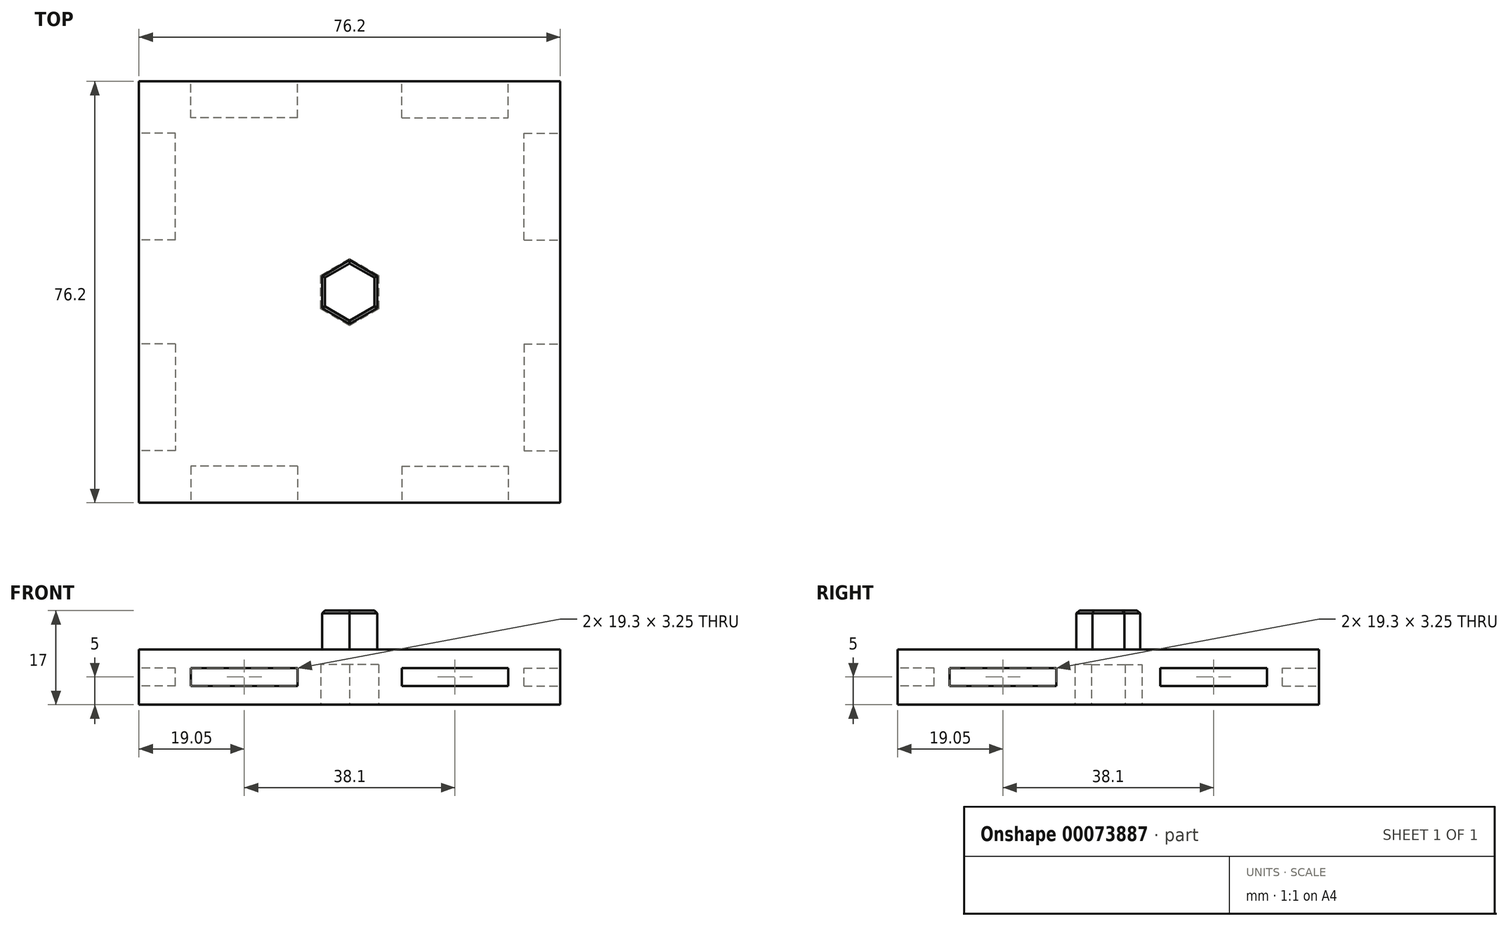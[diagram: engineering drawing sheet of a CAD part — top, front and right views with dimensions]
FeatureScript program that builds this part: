
annotation { "Feature Type Name" : "Feature", "Feature Type Description" : "" }
export const myFeature = defineFeature(function(context is Context, id is Id, definition is map)
    precondition{}
    {
        {
            var Q0;
            Q0=qCreatedBy(makeId("Top.planeOp"),FACE);
            var sketch = newSketch(context, id + "F0", { "sketchPlane" : qUnion([Q0])});
            skLineSegment(sketch, "E0.rect.bottom", {"start": v(38.1, -38.1) * mm, "end": v(-38.1, -38.1) * mm});
            skLineSegment(sketch, "E0.rect.top", {"start": v(38.1, 38.1) * mm, "end": v(-38.1, 38.1) * mm});
            skLineSegment(sketch, "E0.rect.left", {"start": v(38.1, -38.1) * mm, "end": v(38.1, 38.1) * mm});
            skLineSegment(sketch, "E0.rect.right", {"start": v(-38.1, -38.1) * mm, "end": v(-38.1, 38.1) * mm});
            skPoint(sketch, "E0.rect.middle", {"position": v(0, 0) * mm});
            skSolve(sketch);
        }
        {
            var Q0;
            Q0=makeQuery(id+"F0.imprint","IMPRINT",FACE,{"disambiguationData":[TD([[makeQuery(id+"F0.imprint","IMPRINT",EDGE,{"derivedFrom":sQuery(id+"F0.wireOp",EDGE,"E0.rect.bottom")}),-1.0]])]});
            extrude(context, id + "F1", {"entities" : qUnion([Q0]), "depth" : 10 * mm});
        }
        {
            var Q0;
            Q0=makeQuery(id+"F1.opExtrude","CAP_FACE",FACE,{"disambiguationData":[OSD([sQuery(id+"F0.wireOp",EDGE,"E0.rect.bottom"),sQuery(id+"F0.wireOp",EDGE,"E0.rect.top"),sQuery(id+"F0.wireOp",EDGE,"E0.rect.left"),sQuery(id+"F0.wireOp",EDGE,"E0.rect.right")])],"isStart":false});
            var sketch = newSketch(context, id + "F2", { "sketchPlane" : qUnion([Q0])});
            skCircle(sketch, "E1.cCircle", {"center": v(0, 0) * mm, "radius": 5 * mm, "construction": true});
            skLineSegment(sketch, "E1.0", {"start": v(5, 2.89) * mm, "end": v(5, -2.89) * mm});
            skLineSegment(sketch, "E1.1", {"start": v(5, -2.89) * mm, "end": v(0, -5.77) * mm});
            skLineSegment(sketch, "E1.2", {"start": v(0, -5.77) * mm, "end": v(-5, -2.89) * mm});
            skLineSegment(sketch, "E1.3", {"start": v(-5, -2.89) * mm, "end": v(-5, 2.89) * mm});
            skLineSegment(sketch, "E1.4", {"start": v(-5, 2.89) * mm, "end": v(0, 5.77) * mm});
            skLineSegment(sketch, "E1.5", {"start": v(0, 5.77) * mm, "end": v(5, 2.89) * mm});
            skPoint(sketch, "E1.0.midPoint", {"position": v(5, 0) * mm});
            skSolve(sketch);
        }
        {
            var Q0;
            Q0=makeQuery(id+"F2.imprint","IMPRINT",FACE,{"disambiguationData":[TD([[makeQuery(id+"F2.imprint","IMPRINT",EDGE,{"derivedFrom":sQuery(id+"F2.wireOp",EDGE,"E1.0")}),-1.0]])]});
            extrude(context, id + "F3", {"entities" : qUnion([Q0]), "operationType" : NewBodyOperationType.ADD, "depth" : 7 * mm});
        }
        {
            var Q0;
            Q0=makeQuery(id+"F1.opExtrude","CAP_FACE",FACE,{"disambiguationData":[OSD([sQuery(id+"F0.wireOp",EDGE,"E0.rect.bottom"),sQuery(id+"F0.wireOp",EDGE,"E0.rect.top"),sQuery(id+"F0.wireOp",EDGE,"E0.rect.left"),sQuery(id+"F0.wireOp",EDGE,"E0.rect.right")])],"isStart":true});
            var sketch = newSketch(context, id + "F4", { "sketchPlane" : qUnion([Q0])});
            skCircle(sketch, "E2.0", {"center": v(0, 0) * mm, "radius": 5 * mm, "construction": true});
            skLineSegment(sketch, "E2.1", {"start": v(5, -2.89) * mm, "end": v(5, 2.89) * mm, "construction": true});
            skLineSegment(sketch, "E2.2", {"start": v(5, 2.89) * mm, "end": v(0, 5.77) * mm, "construction": true});
            skLineSegment(sketch, "E2.3", {"start": v(0, 5.77) * mm, "end": v(-5, 2.89) * mm, "construction": true});
            skLineSegment(sketch, "E2.4", {"start": v(-5, 2.89) * mm, "end": v(-5, -2.89) * mm, "construction": true});
            skLineSegment(sketch, "E2.5", {"start": v(-5, -2.89) * mm, "end": v(0, -5.77) * mm, "construction": true});
            skLineSegment(sketch, "E2.6", {"start": v(0, -5.77) * mm, "end": v(5, -2.89) * mm, "construction": true});
            skPoint(sketch, "E2.7", {"position": v(5, 0) * mm});
            skLineSegment(sketch, "E3.0", {"start": v(5.25, 3.03) * mm, "end": v(0, 6.06) * mm});
            skLineSegment(sketch, "E3.1", {"start": v(-5.25, 3.03) * mm, "end": v(-5.25, -3.03) * mm});
            skLineSegment(sketch, "E3.2", {"start": v(-5.25, -3.03) * mm, "end": v(0, -6.06) * mm});
            skLineSegment(sketch, "E3.3", {"start": v(0, 6.06) * mm, "end": v(-5.25, 3.03) * mm});
            skLineSegment(sketch, "E3.4", {"start": v(0, -6.06) * mm, "end": v(5.25, -3.03) * mm});
            skLineSegment(sketch, "E3.5", {"start": v(5.25, -3.03) * mm, "end": v(5.25, 3.03) * mm});
            skSolve(sketch);
        }
        {
            var Q0;
            Q0 = qSketchRegion(id + "F4", true);
            extrude(context, id + "F5", {"entities" : qUnion([Q0]), "operationType" : NewBodyOperationType.REMOVE, "oppositeDirection" : true, "depth" : 7.25 * mm});
        }
        {
            var Q0;
            Q0=makeQuery(id+"F1.opExtrude","SWEPT_FACE",FACE,{"disambiguationData":[OSD([sQuery(id+"F0.wireOp",EDGE,"E0.rect.bottom")])]});
            var sketch = newSketch(context, id + "F6", { "sketchPlane" : qUnion([Q0])});
            skLineSegment(sketch, "E4", {"start": v(0, 0) * mm, "end": v(0, 5) * mm, "construction": true});
            skLineSegment(sketch, "E5", {"start": v(-6.35, 5) * mm, "end": v(6.35, 5) * mm, "construction": true});
            skLineSegment(sketch, "E6.rect.bottom", {"start": v(-6.35, 0) * mm, "end": v(-31.75, 0) * mm, "construction": true});
            skLineSegment(sketch, "E6.rect.top", {"start": v(-6.35, 10) * mm, "end": v(-31.75, 10) * mm, "construction": true});
            skLineSegment(sketch, "E6.rect.left", {"start": v(-6.35, 0) * mm, "end": v(-6.35, 10) * mm, "construction": true});
            skLineSegment(sketch, "E6.rect.right", {"start": v(-31.75, 0) * mm, "end": v(-31.75, 10) * mm, "construction": true});
            skPoint(sketch, "E6.rect.middle", {"position": v(-19.05, 5) * mm});
            skLineSegment(sketch, "E7", {"start": v(-44.45, 5) * mm, "end": v(-31.75, 5) * mm, "construction": true});
            skPoint(sketch, "E8", {"position": v(-38.1, 5) * mm});
            skLineSegment(sketch, "E9.rect.bottom", {"start": v(-9.4, 3.37) * mm, "end": v(-28.7, 3.37) * mm});
            skLineSegment(sketch, "E9.rect.top", {"start": v(-9.4, 6.62) * mm, "end": v(-28.7, 6.63) * mm});
            skLineSegment(sketch, "E9.rect.left", {"start": v(-9.4, 3.37) * mm, "end": v(-9.4, 6.62) * mm});
            skLineSegment(sketch, "E9.rect.right", {"start": v(-28.7, 3.37) * mm, "end": v(-28.7, 6.62) * mm});
            skPoint(sketch, "E10.MirrorP", {"position": v(19.05, 5) * mm});
            skLineSegment(sketch, "E11.MirrorCS", {"start": v(28.7, 3.37) * mm, "end": v(28.7, 6.62) * mm});
            skLineSegment(sketch, "E12.MirrorCS", {"start": v(9.4, 3.37) * mm, "end": v(9.4, 6.62) * mm});
            skLineSegment(sketch, "E13.MirrorCS", {"start": v(9.4, 3.37) * mm, "end": v(28.7, 3.37) * mm});
            skLineSegment(sketch, "E14.MirrorCS", {"start": v(9.4, 6.62) * mm, "end": v(28.7, 6.63) * mm});
            skSolve(sketch);
        }
        {
            var Q0;
            Q0=qCreatedBy(makeId("Front.planeOp"),FACE);
            var sketch = newSketch(context, id + "F7", { "sketchPlane" : qUnion([Q0])});
            skLineSegment(sketch, "E15", {"start": v(0, 40.14) * mm, "end": v(0, 0) * mm, "construction": true});
            skSolve(sketch);
        }
        {
            var Q0;
            Q0 = qSketchRegion(id + "F6", true);
            extrude(context, id + "F8", {"entities" : qUnion([Q0]), "oppositeDirection" : true, "depth" : 6.35 * mm + .25 * mm});
        }
        {
            var Q0;
            Q0=makeQuery(id+"F8.opExtrude","SWEPT_BODY",BODY,{"disambiguationData":[OSD([sQuery(id+"F6.wireOp",EDGE,"E11.MirrorCS"),sQuery(id+"F6.wireOp",EDGE,"E12.MirrorCS"),sQuery(id+"F6.wireOp",EDGE,"E13.MirrorCS"),sQuery(id+"F6.wireOp",EDGE,"E14.MirrorCS")])]});
            var Q1;
            Q1=makeQuery(id+"F8.opExtrude","SWEPT_BODY",BODY,{"disambiguationData":[OSD([sQuery(id+"F6.wireOp",EDGE,"E9.rect.bottom"),sQuery(id+"F6.wireOp",EDGE,"E9.rect.top"),sQuery(id+"F6.wireOp",EDGE,"E9.rect.left"),sQuery(id+"F6.wireOp",EDGE,"E9.rect.right")])]});
            var Q2;
            Q2=sQuery(id+"F7.wireOp",EDGE,"E15");
            circularPattern(context, id + "F9", {"entities" : qUnion([Q0, Q1]), "axis" : qUnion([Q2]), "angle" : 90 * degree, "instanceCount" : 4});
        }
        {
            var Q0;
            Q0=makeQuery(id+"F9.opPattern","COPY",BODY,{"derivedFrom":makeQuery(id+"F8.opExtrude","SWEPT_BODY",BODY,{"disambiguationData":[OSD([sQuery(id+"F6.wireOp",EDGE,"E11.MirrorCS"),sQuery(id+"F6.wireOp",EDGE,"E12.MirrorCS"),sQuery(id+"F6.wireOp",EDGE,"E13.MirrorCS"),sQuery(id+"F6.wireOp",EDGE,"E14.MirrorCS")])]}),"instanceName":"3"});
            var Q1;
            Q1=makeQuery(id+"F9.opPattern","COPY",BODY,{"derivedFrom":makeQuery(id+"F8.opExtrude","SWEPT_BODY",BODY,{"disambiguationData":[OSD([sQuery(id+"F6.wireOp",EDGE,"E9.rect.bottom"),sQuery(id+"F6.wireOp",EDGE,"E9.rect.top"),sQuery(id+"F6.wireOp",EDGE,"E9.rect.left"),sQuery(id+"F6.wireOp",EDGE,"E9.rect.right")])]}),"instanceName":"3"});
            var Q2;
            Q2=makeQuery(id+"F9.opPattern","COPY",BODY,{"derivedFrom":makeQuery(id+"F8.opExtrude","SWEPT_BODY",BODY,{"disambiguationData":[OSD([sQuery(id+"F6.wireOp",EDGE,"E11.MirrorCS"),sQuery(id+"F6.wireOp",EDGE,"E12.MirrorCS"),sQuery(id+"F6.wireOp",EDGE,"E13.MirrorCS"),sQuery(id+"F6.wireOp",EDGE,"E14.MirrorCS")])]}),"instanceName":"2"});
            var Q3;
            Q3=makeQuery(id+"F9.opPattern","COPY",BODY,{"derivedFrom":makeQuery(id+"F8.opExtrude","SWEPT_BODY",BODY,{"disambiguationData":[OSD([sQuery(id+"F6.wireOp",EDGE,"E9.rect.bottom"),sQuery(id+"F6.wireOp",EDGE,"E9.rect.top"),sQuery(id+"F6.wireOp",EDGE,"E9.rect.left"),sQuery(id+"F6.wireOp",EDGE,"E9.rect.right")])]}),"instanceName":"2"});
            var Q4;
            Q4=makeQuery(id+"F9.opPattern","COPY",BODY,{"derivedFrom":makeQuery(id+"F8.opExtrude","SWEPT_BODY",BODY,{"disambiguationData":[OSD([sQuery(id+"F6.wireOp",EDGE,"E11.MirrorCS"),sQuery(id+"F6.wireOp",EDGE,"E12.MirrorCS"),sQuery(id+"F6.wireOp",EDGE,"E13.MirrorCS"),sQuery(id+"F6.wireOp",EDGE,"E14.MirrorCS")])]}),"instanceName":"1"});
            var Q5;
            Q5=makeQuery(id+"F9.opPattern","COPY",BODY,{"derivedFrom":makeQuery(id+"F8.opExtrude","SWEPT_BODY",BODY,{"disambiguationData":[OSD([sQuery(id+"F6.wireOp",EDGE,"E9.rect.bottom"),sQuery(id+"F6.wireOp",EDGE,"E9.rect.top"),sQuery(id+"F6.wireOp",EDGE,"E9.rect.left"),sQuery(id+"F6.wireOp",EDGE,"E9.rect.right")])]}),"instanceName":"1"});
            var Q6;
            Q6=makeQuery(id+"F8.opExtrude","SWEPT_BODY",BODY,{"disambiguationData":[OSD([sQuery(id+"F6.wireOp",EDGE,"E11.MirrorCS"),sQuery(id+"F6.wireOp",EDGE,"E12.MirrorCS"),sQuery(id+"F6.wireOp",EDGE,"E13.MirrorCS"),sQuery(id+"F6.wireOp",EDGE,"E14.MirrorCS")])]});
            var Q7;
            Q7=makeQuery(id+"F8.opExtrude","SWEPT_BODY",BODY,{"disambiguationData":[OSD([sQuery(id+"F6.wireOp",EDGE,"E9.rect.bottom"),sQuery(id+"F6.wireOp",EDGE,"E9.rect.top"),sQuery(id+"F6.wireOp",EDGE,"E9.rect.left"),sQuery(id+"F6.wireOp",EDGE,"E9.rect.right")])]});
            var Q8;
            Q8=makeQuery(id+"F1.opExtrude","SWEPT_BODY",BODY,{"disambiguationData":[OSD([sQuery(id+"F0.wireOp",EDGE,"E0.rect.bottom"),sQuery(id+"F0.wireOp",EDGE,"E0.rect.top"),sQuery(id+"F0.wireOp",EDGE,"E0.rect.left"),sQuery(id+"F0.wireOp",EDGE,"E0.rect.right")])]});
            booleanBodies(context, id + "F10", {"operationType" : BooleanOperationType.SUBTRACTION, "tools" : qUnion([Q0, Q1, Q2, Q3, Q4, Q5, Q6, Q7]), "targets" : qUnion([Q8])});
        }
        {
            var Q0;
            Q0=makeQuery(id+"F3.opExtrude","CAP_FACE",FACE,{"disambiguationData":[OSD([sQuery(id+"F2.wireOp",EDGE,"E1.0"),sQuery(id+"F2.wireOp",EDGE,"E1.1"),sQuery(id+"F2.wireOp",EDGE,"E1.2"),sQuery(id+"F2.wireOp",EDGE,"E1.3"),sQuery(id+"F2.wireOp",EDGE,"E1.4"),sQuery(id+"F2.wireOp",EDGE,"E1.5")])],"isStart":false});
            var Q1;
            Q1=makeQuery(id+"F5.boolean.opBoolean","COPY",EDGE,{"derivedFrom":makeQuery(id+"F5.opExtrude","CAP_EDGE",EDGE,{"disambiguationData":[OSD([sQuery(id+"F4.wireOp",EDGE,"E3.4")])],"isStart":true})});
            var Q2;
            Q2=makeQuery(id+"F5.boolean.opBoolean","COPY",EDGE,{"derivedFrom":makeQuery(id+"F5.opExtrude","CAP_EDGE",EDGE,{"disambiguationData":[OSD([sQuery(id+"F4.wireOp",EDGE,"E3.5")])],"isStart":true})});
            var Q3;
            Q3=makeQuery(id+"F5.boolean.opBoolean","COPY",EDGE,{"derivedFrom":makeQuery(id+"F5.opExtrude","CAP_EDGE",EDGE,{"disambiguationData":[OSD([sQuery(id+"F4.wireOp",EDGE,"E3.0")])],"isStart":true})});
            var Q4;
            Q4=makeQuery(id+"F5.boolean.opBoolean","COPY",EDGE,{"derivedFrom":makeQuery(id+"F5.opExtrude","CAP_EDGE",EDGE,{"disambiguationData":[OSD([sQuery(id+"F4.wireOp",EDGE,"E3.3")])],"isStart":true})});
            var Q5;
            Q5=makeQuery(id+"F5.boolean.opBoolean","COPY",EDGE,{"derivedFrom":makeQuery(id+"F5.opExtrude","CAP_EDGE",EDGE,{"disambiguationData":[OSD([sQuery(id+"F4.wireOp",EDGE,"E3.1")])],"isStart":true})});
            var Q6;
            Q6=makeQuery(id+"F5.boolean.opBoolean","COPY",EDGE,{"derivedFrom":makeQuery(id+"F5.opExtrude","CAP_EDGE",EDGE,{"disambiguationData":[OSD([sQuery(id+"F4.wireOp",EDGE,"E3.2")])],"isStart":true})});
            var Q7;
            Q7=makeQuery(id+"F10.opBoolean","COPY",EDGE,{"derivedFrom":makeQuery(id+"F9.opPattern","COPY",EDGE,{"derivedFrom":makeQuery(id+"F8.opExtrude","CAP_EDGE",EDGE,{"disambiguationData":[OSD([sQuery(id+"F6.wireOp",EDGE,"E9.rect.top")])],"isStart":true}),"instanceName":"3"})});
            var Q8;
            Q8=makeQuery(id+"F10.opBoolean","COPY",EDGE,{"derivedFrom":makeQuery(id+"F9.opPattern","COPY",EDGE,{"derivedFrom":makeQuery(id+"F8.opExtrude","CAP_EDGE",EDGE,{"disambiguationData":[OSD([sQuery(id+"F6.wireOp",EDGE,"E9.rect.left")])],"isStart":true}),"instanceName":"3"})});
            var Q9;
            Q9=makeQuery(id+"F10.opBoolean","COPY",EDGE,{"derivedFrom":makeQuery(id+"F9.opPattern","COPY",EDGE,{"derivedFrom":makeQuery(id+"F8.opExtrude","CAP_EDGE",EDGE,{"disambiguationData":[OSD([sQuery(id+"F6.wireOp",EDGE,"E9.rect.bottom")])],"isStart":true}),"instanceName":"3"})});
            var Q10;
            Q10=makeQuery(id+"F10.opBoolean","COPY",EDGE,{"derivedFrom":makeQuery(id+"F9.opPattern","COPY",EDGE,{"derivedFrom":makeQuery(id+"F8.opExtrude","CAP_EDGE",EDGE,{"disambiguationData":[OSD([sQuery(id+"F6.wireOp",EDGE,"E9.rect.right")])],"isStart":true}),"instanceName":"3"})});
            var Q11;
            Q11=makeQuery(id+"F10.opBoolean","COPY",EDGE,{"derivedFrom":makeQuery(id+"F9.opPattern","COPY",EDGE,{"derivedFrom":makeQuery(id+"F8.opExtrude","CAP_EDGE",EDGE,{"disambiguationData":[OSD([sQuery(id+"F6.wireOp",EDGE,"E13.MirrorCS")])],"isStart":true}),"instanceName":"3"})});
            var Q12;
            Q12=makeQuery(id+"F10.opBoolean","COPY",EDGE,{"derivedFrom":makeQuery(id+"F9.opPattern","COPY",EDGE,{"derivedFrom":makeQuery(id+"F8.opExtrude","CAP_EDGE",EDGE,{"disambiguationData":[OSD([sQuery(id+"F6.wireOp",EDGE,"E12.MirrorCS")])],"isStart":true}),"instanceName":"3"})});
            var Q13;
            Q13=makeQuery(id+"F10.opBoolean","COPY",EDGE,{"derivedFrom":makeQuery(id+"F9.opPattern","COPY",EDGE,{"derivedFrom":makeQuery(id+"F8.opExtrude","CAP_EDGE",EDGE,{"disambiguationData":[OSD([sQuery(id+"F6.wireOp",EDGE,"E11.MirrorCS")])],"isStart":true}),"instanceName":"3"})});
            var Q14;
            Q14=makeQuery(id+"F10.opBoolean","COPY",EDGE,{"derivedFrom":makeQuery(id+"F9.opPattern","COPY",EDGE,{"derivedFrom":makeQuery(id+"F8.opExtrude","CAP_EDGE",EDGE,{"disambiguationData":[OSD([sQuery(id+"F6.wireOp",EDGE,"E14.MirrorCS")])],"isStart":true}),"instanceName":"3"})});
            var Q15;
            Q15=makeQuery(id+"F10.opBoolean","COPY",EDGE,{"derivedFrom":makeQuery(id+"F9.opPattern","COPY",EDGE,{"derivedFrom":makeQuery(id+"F8.opExtrude","CAP_EDGE",EDGE,{"disambiguationData":[OSD([sQuery(id+"F6.wireOp",EDGE,"E9.rect.top")])],"isStart":true}),"instanceName":"2"})});
            var Q16;
            Q16=makeQuery(id+"F10.opBoolean","COPY",EDGE,{"derivedFrom":makeQuery(id+"F9.opPattern","COPY",EDGE,{"derivedFrom":makeQuery(id+"F8.opExtrude","CAP_EDGE",EDGE,{"disambiguationData":[OSD([sQuery(id+"F6.wireOp",EDGE,"E9.rect.right")])],"isStart":true}),"instanceName":"2"})});
            var Q17;
            Q17=makeQuery(id+"F10.opBoolean","COPY",EDGE,{"derivedFrom":makeQuery(id+"F9.opPattern","COPY",EDGE,{"derivedFrom":makeQuery(id+"F8.opExtrude","CAP_EDGE",EDGE,{"disambiguationData":[OSD([sQuery(id+"F6.wireOp",EDGE,"E9.rect.left")])],"isStart":true}),"instanceName":"2"})});
            var Q18;
            Q18=makeQuery(id+"F10.opBoolean","COPY",EDGE,{"derivedFrom":makeQuery(id+"F9.opPattern","COPY",EDGE,{"derivedFrom":makeQuery(id+"F8.opExtrude","CAP_EDGE",EDGE,{"disambiguationData":[OSD([sQuery(id+"F6.wireOp",EDGE,"E9.rect.bottom")])],"isStart":true}),"instanceName":"2"})});
            var Q19;
            Q19=makeQuery(id+"F10.opBoolean","COPY",EDGE,{"derivedFrom":makeQuery(id+"F8.opExtrude","CAP_EDGE",EDGE,{"disambiguationData":[OSD([sQuery(id+"F6.wireOp",EDGE,"E11.MirrorCS")])],"isStart":true})});
            var Q20;
            Q20=makeQuery(id+"F10.opBoolean","COPY",EDGE,{"derivedFrom":makeQuery(id+"F8.opExtrude","CAP_EDGE",EDGE,{"disambiguationData":[OSD([sQuery(id+"F6.wireOp",EDGE,"E14.MirrorCS")])],"isStart":true})});
            var Q21;
            Q21=makeQuery(id+"F10.opBoolean","COPY",EDGE,{"derivedFrom":makeQuery(id+"F8.opExtrude","CAP_EDGE",EDGE,{"disambiguationData":[OSD([sQuery(id+"F6.wireOp",EDGE,"E12.MirrorCS")])],"isStart":true})});
            var Q22;
            Q22=makeQuery(id+"F10.opBoolean","COPY",EDGE,{"derivedFrom":makeQuery(id+"F8.opExtrude","CAP_EDGE",EDGE,{"disambiguationData":[OSD([sQuery(id+"F6.wireOp",EDGE,"E13.MirrorCS")])],"isStart":true})});
            var Q23;
            Q23=makeQuery(id+"F10.opBoolean","COPY",EDGE,{"derivedFrom":makeQuery(id+"F8.opExtrude","CAP_EDGE",EDGE,{"disambiguationData":[OSD([sQuery(id+"F6.wireOp",EDGE,"E9.rect.left")])],"isStart":true})});
            var Q24;
            Q24=makeQuery(id+"F10.opBoolean","COPY",EDGE,{"derivedFrom":makeQuery(id+"F8.opExtrude","CAP_EDGE",EDGE,{"disambiguationData":[OSD([sQuery(id+"F6.wireOp",EDGE,"E9.rect.top")])],"isStart":true})});
            var Q25;
            Q25=makeQuery(id+"F10.opBoolean","COPY",EDGE,{"derivedFrom":makeQuery(id+"F8.opExtrude","CAP_EDGE",EDGE,{"disambiguationData":[OSD([sQuery(id+"F6.wireOp",EDGE,"E9.rect.bottom")])],"isStart":true})});
            var Q26;
            Q26=makeQuery(id+"F10.opBoolean","COPY",EDGE,{"derivedFrom":makeQuery(id+"F8.opExtrude","CAP_EDGE",EDGE,{"disambiguationData":[OSD([sQuery(id+"F6.wireOp",EDGE,"E9.rect.right")])],"isStart":true})});
            var Q27;
            Q27=makeQuery(id+"F10.opBoolean","COPY",EDGE,{"derivedFrom":makeQuery(id+"F9.opPattern","COPY",EDGE,{"derivedFrom":makeQuery(id+"F8.opExtrude","CAP_EDGE",EDGE,{"disambiguationData":[OSD([sQuery(id+"F6.wireOp",EDGE,"E11.MirrorCS")])],"isStart":true}),"instanceName":"1"})});
            var Q28;
            Q28=makeQuery(id+"F10.opBoolean","COPY",EDGE,{"derivedFrom":makeQuery(id+"F9.opPattern","COPY",EDGE,{"derivedFrom":makeQuery(id+"F8.opExtrude","CAP_EDGE",EDGE,{"disambiguationData":[OSD([sQuery(id+"F6.wireOp",EDGE,"E14.MirrorCS")])],"isStart":true}),"instanceName":"1"})});
            var Q29;
            Q29=makeQuery(id+"F10.opBoolean","COPY",EDGE,{"derivedFrom":makeQuery(id+"F9.opPattern","COPY",EDGE,{"derivedFrom":makeQuery(id+"F8.opExtrude","CAP_EDGE",EDGE,{"disambiguationData":[OSD([sQuery(id+"F6.wireOp",EDGE,"E12.MirrorCS")])],"isStart":true}),"instanceName":"1"})});
            var Q30;
            Q30=makeQuery(id+"F10.opBoolean","COPY",EDGE,{"derivedFrom":makeQuery(id+"F9.opPattern","COPY",EDGE,{"derivedFrom":makeQuery(id+"F8.opExtrude","CAP_EDGE",EDGE,{"disambiguationData":[OSD([sQuery(id+"F6.wireOp",EDGE,"E13.MirrorCS")])],"isStart":true}),"instanceName":"1"})});
            var Q31;
            Q31=makeQuery(id+"F10.opBoolean","COPY",EDGE,{"derivedFrom":makeQuery(id+"F9.opPattern","COPY",EDGE,{"derivedFrom":makeQuery(id+"F8.opExtrude","CAP_EDGE",EDGE,{"disambiguationData":[OSD([sQuery(id+"F6.wireOp",EDGE,"E9.rect.left")])],"isStart":true}),"instanceName":"1"})});
            var Q32;
            Q32=makeQuery(id+"F10.opBoolean","COPY",EDGE,{"derivedFrom":makeQuery(id+"F9.opPattern","COPY",EDGE,{"derivedFrom":makeQuery(id+"F8.opExtrude","CAP_EDGE",EDGE,{"disambiguationData":[OSD([sQuery(id+"F6.wireOp",EDGE,"E9.rect.top")])],"isStart":true}),"instanceName":"1"})});
            var Q33;
            Q33=makeQuery(id+"F10.opBoolean","COPY",EDGE,{"derivedFrom":makeQuery(id+"F9.opPattern","COPY",EDGE,{"derivedFrom":makeQuery(id+"F8.opExtrude","CAP_EDGE",EDGE,{"disambiguationData":[OSD([sQuery(id+"F6.wireOp",EDGE,"E9.rect.right")])],"isStart":true}),"instanceName":"1"})});
            var Q34;
            Q34=makeQuery(id+"F10.opBoolean","COPY",EDGE,{"derivedFrom":makeQuery(id+"F9.opPattern","COPY",EDGE,{"derivedFrom":makeQuery(id+"F8.opExtrude","CAP_EDGE",EDGE,{"disambiguationData":[OSD([sQuery(id+"F6.wireOp",EDGE,"E9.rect.bottom")])],"isStart":true}),"instanceName":"1"})});
            var Q35;
            Q35=makeQuery(id+"F10.opBoolean","COPY",EDGE,{"derivedFrom":makeQuery(id+"F9.opPattern","COPY",EDGE,{"derivedFrom":makeQuery(id+"F8.opExtrude","CAP_EDGE",EDGE,{"disambiguationData":[OSD([sQuery(id+"F6.wireOp",EDGE,"E14.MirrorCS")])],"isStart":true}),"instanceName":"2"})});
            var Q36;
            Q36=makeQuery(id+"F10.opBoolean","COPY",EDGE,{"derivedFrom":makeQuery(id+"F9.opPattern","COPY",EDGE,{"derivedFrom":makeQuery(id+"F8.opExtrude","CAP_EDGE",EDGE,{"disambiguationData":[OSD([sQuery(id+"F6.wireOp",EDGE,"E11.MirrorCS")])],"isStart":true}),"instanceName":"2"})});
            var Q37;
            Q37=makeQuery(id+"F10.opBoolean","COPY",EDGE,{"derivedFrom":makeQuery(id+"F9.opPattern","COPY",EDGE,{"derivedFrom":makeQuery(id+"F8.opExtrude","CAP_EDGE",EDGE,{"disambiguationData":[OSD([sQuery(id+"F6.wireOp",EDGE,"E12.MirrorCS")])],"isStart":true}),"instanceName":"2"})});
            var Q38;
            Q38=makeQuery(id+"F10.opBoolean","COPY",EDGE,{"derivedFrom":makeQuery(id+"F9.opPattern","COPY",EDGE,{"derivedFrom":makeQuery(id+"F8.opExtrude","CAP_EDGE",EDGE,{"disambiguationData":[OSD([sQuery(id+"F6.wireOp",EDGE,"E13.MirrorCS")])],"isStart":true}),"instanceName":"2"})});
            chamfer(context, id + "F11", {"entities" : qUnion([Q0, Q1, Q2, Q3, Q4, Q5, Q6, Q7, Q8, Q9, Q10, Q11, Q12, Q13, Q14, Q15, Q16, Q17, Q18, Q19, Q20, Q21, Q22, Q23, Q24, Q25, Q26, Q27, Q28, Q29, Q30, Q31, Q32, Q33, Q34, Q35, Q36, Q37, Q38]), "width" : .5 * mm, "tangentPropagation" : true});
        }
        {
            var Q0;
            Q0=qCreatedBy(makeId("Right.planeOp"),FACE);
            var sketch = newSketch(context, id + "F12", { "sketchPlane" : qUnion([Q0])});
            skLineSegment(sketch, "E16", {"start": v(0, 17) * mm, "end": v(0, 7) * mm, "construction": true});
            skSolve(sketch);
        }
        {
            var Q0;
            Q0=makeQuery(id+"F1.opExtrude","SWEPT_FACE",FACE,{"disambiguationData":[OSD([sQuery(id+"F0.wireOp",EDGE,"E0.rect.bottom")])]});
            var sketch = newSketch(context, id + "F13", { "sketchPlane" : qUnion([Q0])});
            skLineSegment(sketch, "E17.bottom", {"start": v(8.9, 2.87) * mm, "end": v(29.2, 2.87) * mm});
            skLineSegment(sketch, "E17.top", {"start": v(8.9, 7.12) * mm, "end": v(29.2, 7.12) * mm});
            skLineSegment(sketch, "E17.left", {"start": v(8.9, 2.87) * mm, "end": v(8.9, 7.12) * mm});
            skLineSegment(sketch, "E17.right", {"start": v(29.2, 2.87) * mm, "end": v(29.2, 7.12) * mm});
            skPoint(sketch, "E17.middle", {"position": v(19.05, 5) * mm});
            skPoint(sketch, "E17.middle.positionSnap0", {"position": v(19.05, 2.87) * mm});
            skPoint(sketch, "E17.middle.positionSnap1", {"position": v(8.9, 5) * mm});
            skPoint(sketch, "E17.centerSnap0", {"position": v(19.05, 2.87) * mm});
            skPoint(sketch, "E17.centerSnap1", {"position": v(8.9, 5) * mm});
            skLineSegment(sketch, "E18.bottom", {"start": v(-8.9, 2.87) * mm, "end": v(-29.2, 2.87) * mm});
            skLineSegment(sketch, "E18.top", {"start": v(-8.9, 7.12) * mm, "end": v(-29.2, 7.12) * mm});
            skLineSegment(sketch, "E18.left", {"start": v(-8.9, 2.87) * mm, "end": v(-8.9, 7.12) * mm});
            skLineSegment(sketch, "E18.right", {"start": v(-29.2, 2.87) * mm, "end": v(-29.2, 7.12) * mm});
            skPoint(sketch, "E18.middle", {"position": v(-19.05, 5) * mm});
            skPoint(sketch, "E18.middle.positionSnap0", {"position": v(-8.9, 5) * mm});
            skPoint(sketch, "E18.middle.positionSnap1", {"position": v(-19.05, 2.87) * mm});
            skPoint(sketch, "E18.centerSnap0", {"position": v(-8.9, 5) * mm});
            skPoint(sketch, "E18.centerSnap1", {"position": v(-19.05, 2.87) * mm});
            skSolve(sketch);
        }
        {
            var Q0;
            Q0=makeQuery(id+"F1.opExtrude","SWEPT_FACE",FACE,{"disambiguationData":[OSD([sQuery(id+"F0.wireOp",EDGE,"E0.rect.left")])]});
            var sketch = newSketch(context, id + "F14", { "sketchPlane" : qUnion([Q0])});
            skLineSegment(sketch, "E19.bottom", {"start": v(-29.2, 7.13) * mm, "end": v(-8.9, 7.13) * mm});
            skLineSegment(sketch, "E19.top", {"start": v(-29.2, 2.87) * mm, "end": v(-8.9, 2.87) * mm});
            skLineSegment(sketch, "E19.left", {"start": v(-29.2, 7.13) * mm, "end": v(-29.2, 2.87) * mm});
            skLineSegment(sketch, "E19.right", {"start": v(-8.9, 7.13) * mm, "end": v(-8.9, 2.87) * mm});
            skPoint(sketch, "E19.middle", {"position": v(-19.05, 5) * mm});
            skLineSegment(sketch, "E20.bottom", {"start": v(8.9, 7.13) * mm, "end": v(29.2, 7.13) * mm});
            skLineSegment(sketch, "E20.top", {"start": v(8.9, 2.87) * mm, "end": v(29.2, 2.87) * mm});
            skLineSegment(sketch, "E20.left", {"start": v(8.9, 7.13) * mm, "end": v(8.9, 2.87) * mm});
            skLineSegment(sketch, "E20.right", {"start": v(29.2, 7.13) * mm, "end": v(29.2, 2.87) * mm});
            skPoint(sketch, "E20.middle", {"position": v(19.05, 5) * mm});
            skPoint(sketch, "E20.middle.positionSnap0", {"position": v(29.2, 5) * mm});
            skPoint(sketch, "E20.middle.positionSnap1", {"position": v(19.05, 7.13) * mm});
            skPoint(sketch, "E20.centerSnap0", {"position": v(29.2, 5) * mm});
            skPoint(sketch, "E20.centerSnap1", {"position": v(19.05, 7.13) * mm});
            skSolve(sketch);
        }
        {
            var Q0;
            Q0=makeQuery(id+"F1.opExtrude","SWEPT_FACE",FACE,{"disambiguationData":[OSD([sQuery(id+"F0.wireOp",EDGE,"E0.rect.top")])]});
            var sketch = newSketch(context, id + "F15", { "sketchPlane" : qUnion([Q0])});
            skLineSegment(sketch, "E21.bottom", {"start": v(-29.2, 2.88) * mm, "end": v(-8.9, 2.88) * mm});
            skLineSegment(sketch, "E21.top", {"start": v(-29.2, 7.13) * mm, "end": v(-8.9, 7.13) * mm});
            skLineSegment(sketch, "E21.left", {"start": v(-29.2, 2.88) * mm, "end": v(-29.2, 7.13) * mm});
            skLineSegment(sketch, "E21.right", {"start": v(-8.9, 2.88) * mm, "end": v(-8.9, 7.13) * mm});
            skPoint(sketch, "E21.middle", {"position": v(-19.05, 5) * mm});
            skPoint(sketch, "E21.middle.positionSnap0", {"position": v(-29.2, 5) * mm});
            skPoint(sketch, "E21.middle.positionSnap1", {"position": v(-19.05, 7.13) * mm});
            skPoint(sketch, "E21.centerSnap0", {"position": v(-29.2, 5) * mm});
            skPoint(sketch, "E21.centerSnap1", {"position": v(-19.05, 7.13) * mm});
            skLineSegment(sketch, "E22.bottom", {"start": v(8.9, 2.87) * mm, "end": v(29.2, 2.87) * mm});
            skLineSegment(sketch, "E22.top", {"start": v(8.9, 7.12) * mm, "end": v(29.2, 7.12) * mm});
            skLineSegment(sketch, "E22.left", {"start": v(8.9, 2.87) * mm, "end": v(8.9, 7.12) * mm});
            skLineSegment(sketch, "E22.right", {"start": v(29.2, 2.87) * mm, "end": v(29.2, 7.12) * mm});
            skPoint(sketch, "E22.middle", {"position": v(19.05, 5) * mm});
            skPoint(sketch, "E22.middle.positionSnap0", {"position": v(19.05, 7.12) * mm});
            skPoint(sketch, "E22.middle.positionSnap1", {"position": v(8.9, 5) * mm});
            skPoint(sketch, "E22.centerSnap0", {"position": v(19.05, 7.12) * mm});
            skPoint(sketch, "E22.centerSnap1", {"position": v(8.9, 5) * mm});
            skSolve(sketch);
        }
        {
            var Q0;
            Q0=makeQuery(id+"F1.opExtrude","SWEPT_FACE",FACE,{"disambiguationData":[OSD([sQuery(id+"F0.wireOp",EDGE,"E0.rect.right")])]});
            var sketch = newSketch(context, id + "F16", { "sketchPlane" : qUnion([Q0])});
            skLineSegment(sketch, "E23.bottom", {"start": v(-29.2, 7.12) * mm, "end": v(-8.9, 7.12) * mm});
            skLineSegment(sketch, "E23.top", {"start": v(-29.2, 2.87) * mm, "end": v(-8.9, 2.87) * mm});
            skLineSegment(sketch, "E23.left", {"start": v(-29.2, 7.12) * mm, "end": v(-29.2, 2.87) * mm});
            skLineSegment(sketch, "E23.right", {"start": v(-8.9, 7.12) * mm, "end": v(-8.9, 2.87) * mm});
            skPoint(sketch, "E23.middle", {"position": v(-19.05, 5) * mm});
            skPoint(sketch, "E23.middle.positionSnap0", {"position": v(-19.05, 7.12) * mm});
            skPoint(sketch, "E23.middle.positionSnap1", {"position": v(-29.2, 5) * mm});
            skPoint(sketch, "E23.centerSnap0", {"position": v(-19.05, 7.12) * mm});
            skPoint(sketch, "E23.centerSnap1", {"position": v(-29.2, 5) * mm});
            skLineSegment(sketch, "E24.bottom", {"start": v(8.9, 7.12) * mm, "end": v(29.2, 7.12) * mm});
            skLineSegment(sketch, "E24.top", {"start": v(8.9, 2.87) * mm, "end": v(29.2, 2.87) * mm});
            skLineSegment(sketch, "E24.left", {"start": v(8.9, 7.12) * mm, "end": v(8.9, 2.87) * mm});
            skLineSegment(sketch, "E24.right", {"start": v(29.2, 7.12) * mm, "end": v(29.2, 2.87) * mm});
            skPoint(sketch, "E24.middle", {"position": v(19.05, 5) * mm});
            skPoint(sketch, "E24.middle.positionSnap0", {"position": v(19.05, 7.12) * mm});
            skPoint(sketch, "E24.middle.positionSnap1", {"position": v(8.9, 5) * mm});
            skPoint(sketch, "E24.centerSnap0", {"position": v(19.05, 7.12) * mm});
            skPoint(sketch, "E24.centerSnap1", {"position": v(8.9, 5) * mm});
            skSolve(sketch);
        }
    });
